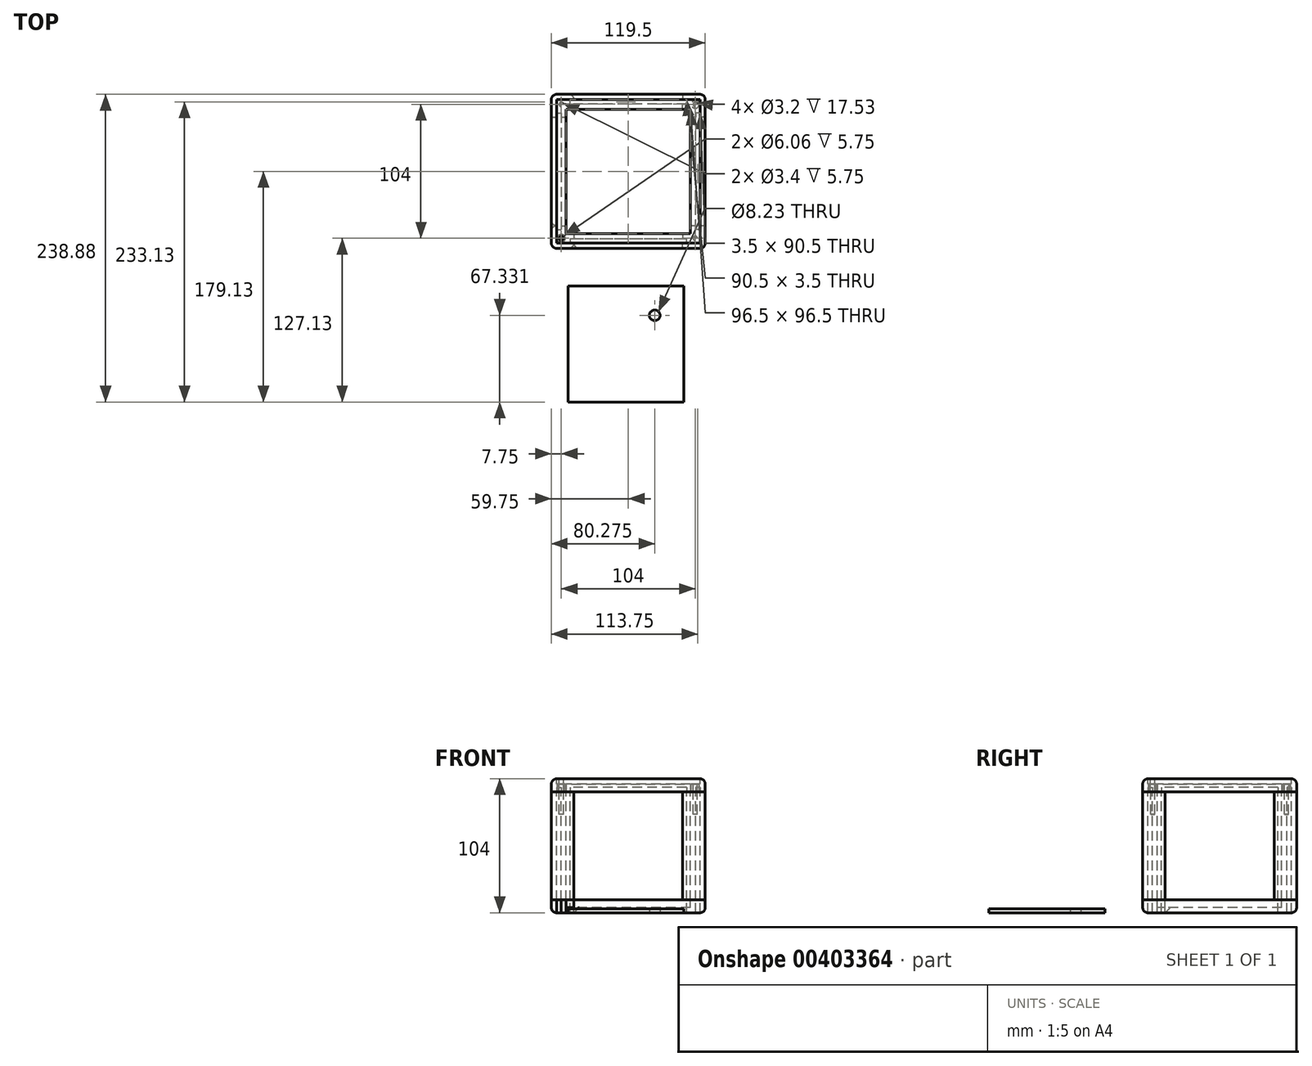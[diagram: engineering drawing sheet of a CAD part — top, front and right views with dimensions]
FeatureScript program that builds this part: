
annotation { "Feature Type Name" : "Feature", "Feature Type Description" : "" }
export const myFeature = defineFeature(function(context is Context, id is Id, definition is map)
    precondition{}
    {
        {
            assignVariable(context, id + "F0", {"name" : "lithophaneHeight", "anyValue" : 90});
        }
        {
            assignVariable(context, id + "F1", {"name" : "lithophaneThickness", "anyValue" : 3});
        }
        {
            assignVariable(context, id + "F2", {"name" : "lithophaneBorderWidth", "anyValue" : 3});
        }
        {
            assignVariable(context, id + "F3", {"name" : "slotToleranceWidth", "anyValue" : .5});
        }
        {
            assignVariable(context, id + "F4", {"name" : "shellThickness", "anyValue" : 4});
        }
        {
            assignVariable(context, id + "F5", {"name" : "baseThickness", "anyValue" : 10});
        }
        {
            assignVariable(context, id + "F6", {"name" : "topThickness", "anyValue" : getVariable(context, 'baseThickness')});
        }
        {
            assignVariable(context, id + "F7", {"name" : "MainEdgeFilletRadius", "anyValue" : 4});
        }
        {
            assignVariable(context, id + "F8", {"name" : "screwThreadDepth", "anyValue" : 19.53});
        }
        {
            assignVariable(context, id + "F9", {"name" : "screwHeadDepth", "anyValue" : 3});
        }
        {
            assignVariable(context, id + "F10", {"name" : "screwHeadRecessTolerance", "anyValue" : 1});
        }
        {
            assignVariable(context, id + "F11", {"name" : "screwHeadSupportThickness", "anyValue" : .25});
        }
        {
            assignVariable(context, id + "F12", {"name" : "screwThreadExtraDepth", "anyValue" : 5});
        }
        {
            var Q0;
            Q0=qCreatedBy(makeId("Top.planeOp"),FACE);
            var sketch = newSketch(context, id + "F13", { "sketchPlane" : qUnion([Q0])});
            skLineSegment(sketch, "E0.bottom", {"start": v(59.75, 59.75) * mm, "end": v(-59.75, 59.75) * mm});
            skLineSegment(sketch, "E0.top", {"start": v(59.75, -59.75) * mm, "end": v(-59.75, -59.75) * mm});
            skLineSegment(sketch, "E0.left", {"start": v(59.75, 59.75) * mm, "end": v(59.75, -59.75) * mm});
            skLineSegment(sketch, "E0.right", {"start": v(-59.75, 59.75) * mm, "end": v(-59.75, -59.75) * mm});
            skPoint(sketch, "E0.middle", {"position": v(0, 0) * mm});
            skSolve(sketch);
        }
        {
            var Q0;
            Q0=makeQuery(id+"F13.imprint","IMPRINT",FACE,{"disambiguationData":[TD([[makeQuery(id+"F13.imprint","IMPRINT",EDGE,{"derivedFrom":sQuery(id+"F13.wireOp",EDGE,"E0.bottom")}),1.0]])]});
            extrude(context, id + "F14", {"entities" : qUnion([Q0]), "depth" : (getVariable(context, 'lithophaneHeight') - (getVariable(context, 'lithophaneBorderWidth') * 2)) * mm});
        }
        {
            var Q0;
            Q0=makeQuery(id+"F14.opExtrude","CAP_FACE",FACE,{"disambiguationData":[OSD([sQuery(id+"F13.wireOp",EDGE,"E0.bottom"),sQuery(id+"F13.wireOp",EDGE,"E0.top"),sQuery(id+"F13.wireOp",EDGE,"E0.left"),sQuery(id+"F13.wireOp",EDGE,"E0.right")])],"isStart":false});
            var sketch = newSketch(context, id + "F15", { "sketchPlane" : qUnion([Q0])});
            skLineSegment(sketch, "E1", {"start": v(-55.75, -59.75) * mm, "end": v(-55.75, 59.75) * mm, "construction": true});
            skLineSegment(sketch, "E2", {"start": v(55.75, -59.75) * mm, "end": v(55.75, 59.75) * mm, "construction": true});
            skLineSegment(sketch, "E3", {"start": v(-59.75, 55.75) * mm, "end": v(59.75, 55.75) * mm, "construction": true});
            skLineSegment(sketch, "E4", {"start": v(-59.75, -55.75) * mm, "end": v(59.75, -55.75) * mm, "construction": true});
            skLineSegment(sketch, "E5", {"start": v(-59.75, 52.25) * mm, "end": v(59.75, 52.25) * mm, "construction": true});
            skLineSegment(sketch, "E6", {"start": v(-59.75, -52.25) * mm, "end": v(59.75, -52.25) * mm, "construction": true});
            skLineSegment(sketch, "E7", {"start": v(52.25, 59.75) * mm, "end": v(52.25, -59.75) * mm, "construction": true});
            skLineSegment(sketch, "E8", {"start": v(-52.25, 59.75) * mm, "end": v(-52.25, -59.75) * mm, "construction": true});
            skLineSegment(sketch, "E9", {"start": v(0, 59.75) * mm, "end": v(0, -59.75) * mm, "construction": true});
            skLineSegment(sketch, "E10", {"start": v(-59.75, 0) * mm, "end": v(59.75, 0) * mm, "construction": true});
            skLineSegment(sketch, "E11", {"start": v(-55.75, 45.25) * mm, "end": v(-52.25, 45.25) * mm});
            skLineSegment(sketch, "E12", {"start": v(-55.75, -45.25) * mm, "end": v(-52.25, -45.25) * mm});
            skPoint(sketch, "E13", {"position": v(-52.25, 0) * mm});
            skPoint(sketch, "E14", {"position": v(-55.75, 0) * mm});
            skLineSegment(sketch, "E15", {"start": v(-55.75, 45.25) * mm, "end": v(-55.75, -45.25) * mm});
            skLineSegment(sketch, "E16", {"start": v(-52.25, 45.25) * mm, "end": v(-52.25, -45.25) * mm});
            skLineSegment(sketch, "E17.MirrorCS", {"start": v(55.75, 45.25) * mm, "end": v(52.25, 45.25) * mm});
            skLineSegment(sketch, "E18.MirrorCS", {"start": v(55.75, -45.25) * mm, "end": v(52.25, -45.25) * mm});
            skLineSegment(sketch, "E19", {"start": v(-45.25, -52.25) * mm, "end": v(-45.25, -55.75) * mm});
            skLineSegment(sketch, "E20", {"start": v(45.25, -55.75) * mm, "end": v(45.25, -52.25) * mm});
            skLineSegment(sketch, "E21.MirrorCS", {"start": v(-45.25, 52.25) * mm, "end": v(-45.25, 55.75) * mm});
            skLineSegment(sketch, "E22.MirrorCS", {"start": v(45.25, 55.75) * mm, "end": v(45.25, 52.25) * mm});
            skLineSegment(sketch, "E23", {"start": v(-45.25, 52.25) * mm, "end": v(45.25, 52.25) * mm});
            skLineSegment(sketch, "E24", {"start": v(-45.25, 55.75) * mm, "end": v(45.25, 55.75) * mm});
            skLineSegment(sketch, "E25", {"start": v(52.25, 45.25) * mm, "end": v(52.25, -45.25) * mm});
            skLineSegment(sketch, "E26", {"start": v(55.75, 45.25) * mm, "end": v(55.75, -45.25) * mm});
            skLineSegment(sketch, "E27", {"start": v(-45.25, -52.25) * mm, "end": v(45.25, -52.25) * mm});
            skLineSegment(sketch, "E28", {"start": v(45.25, -55.75) * mm, "end": v(-45.25, -55.75) * mm});
            skLineSegment(sketch, "E29", {"start": v(-59.75, -42.25) * mm, "end": v(-55.75, -42.25) * mm});
            skLineSegment(sketch, "E30", {"start": v(-59.75, 42.25) * mm, "end": v(-55.75, 42.25) * mm});
            skLineSegment(sketch, "E31", {"start": v(-42.25, -59.75) * mm, "end": v(-42.25, -55.75) * mm});
            skLineSegment(sketch, "E32", {"start": v(42.25, -59.75) * mm, "end": v(42.25, -55.75) * mm});
            skLineSegment(sketch, "E33.MirrorCS", {"start": v(-42.25, 59.75) * mm, "end": v(-42.25, 55.75) * mm});
            skLineSegment(sketch, "E34.MirrorCS", {"start": v(42.25, 59.75) * mm, "end": v(42.25, 55.75) * mm});
            skLineSegment(sketch, "E35.MirrorCS", {"start": v(59.75, 42.25) * mm, "end": v(55.75, 42.25) * mm});
            skLineSegment(sketch, "E36.MirrorCS", {"start": v(59.75, -42.25) * mm, "end": v(55.75, -42.25) * mm});
            skLineSegment(sketch, "E37", {"start": v(-52.25, 42.25) * mm, "end": v(-48.25, 42.25) * mm});
            skLineSegment(sketch, "E38", {"start": v(-48.25, 42.25) * mm, "end": v(-48.25, 48.25) * mm});
            skLineSegment(sketch, "E39", {"start": v(-48.25, 48.25) * mm, "end": v(-42.25, 48.25) * mm});
            skLineSegment(sketch, "E40", {"start": v(-42.25, 48.25) * mm, "end": v(-42.25, 52.25) * mm});
            skLineSegment(sketch, "E41.MirrorCS", {"start": v(42.25, 48.25) * mm, "end": v(42.25, 52.25) * mm});
            skLineSegment(sketch, "E42.MirrorCS", {"start": v(48.25, 48.25) * mm, "end": v(42.25, 48.25) * mm});
            skLineSegment(sketch, "E43.MirrorCS", {"start": v(52.25, 42.25) * mm, "end": v(48.25, 42.25) * mm});
            skLineSegment(sketch, "E44.MirrorCS", {"start": v(48.25, 42.25) * mm, "end": v(48.25, 48.25) * mm});
            skLineSegment(sketch, "E45.MirrorCS", {"start": v(52.25, -42.25) * mm, "end": v(48.25, -42.25) * mm});
            skLineSegment(sketch, "E46.MirrorCS", {"start": v(48.25, -42.25) * mm, "end": v(48.25, -48.25) * mm});
            skLineSegment(sketch, "E47.MirrorCS", {"start": v(48.25, -48.25) * mm, "end": v(42.25, -48.25) * mm});
            skLineSegment(sketch, "E48.MirrorCS", {"start": v(42.25, -48.25) * mm, "end": v(42.25, -52.25) * mm});
            skLineSegment(sketch, "E49.MirrorCS", {"start": v(-42.25, -48.25) * mm, "end": v(-42.25, -52.25) * mm});
            skLineSegment(sketch, "E50.MirrorCS", {"start": v(-48.25, -42.25) * mm, "end": v(-48.25, -48.25) * mm});
            skLineSegment(sketch, "E51.MirrorCS", {"start": v(-52.25, -42.25) * mm, "end": v(-48.25, -42.25) * mm});
            skLineSegment(sketch, "E52.MirrorCS", {"start": v(-48.25, -48.25) * mm, "end": v(-42.25, -48.25) * mm});
            skSolve(sketch);
        }
        {
            var Q0;
            {var subQ4=sQuery(id+"F15.wireOp",EDGE,"E37");Q0=makeQuery(id+"F15.imprint","IMPRINT",FACE,{"disambiguationData":[TD([[makeQuery(id+"F15.imprint","IMPRINT",EDGE,{"derivedFrom":subQ4}),-1.0]])]});}
            var Q1;
            {var subQ3=sQuery(id+"F15.wireOp",EDGE,"E21.MirrorCS");Q1=makeQuery(id+"F15.imprint","IMPRINT",FACE,{"disambiguationData":[TD([[makeQuery(id+"F15.imprint","IMPRINT",EDGE,{"derivedFrom":subQ3}),-1.0]])]});}
            var Q2;
            {var subQ0=sQuery(id+"F15.wireOp",EDGE,"E33.MirrorCS");Q2=makeQuery(id+"F15.imprint","IMPRINT",FACE,{"disambiguationData":[TD([[makeQuery(id+"F15.imprint","IMPRINT",EDGE,{"derivedFrom":subQ0}),1.0]])]});}
            var Q3;
            {var subQ3=sQuery(id+"F15.wireOp",EDGE,"E17.MirrorCS");Q3=makeQuery(id+"F15.imprint","IMPRINT",FACE,{"disambiguationData":[TD([[makeQuery(id+"F15.imprint","IMPRINT",EDGE,{"derivedFrom":subQ3}),1.0]])]});}
            var Q4;
            {var subQ0=sQuery(id+"F15.wireOp",EDGE,"E35.MirrorCS");Q4=makeQuery(id+"F15.imprint","IMPRINT",FACE,{"disambiguationData":[TD([[makeQuery(id+"F15.imprint","IMPRINT",EDGE,{"derivedFrom":subQ0}),1.0]])]});}
            var Q5;
            {var subQ3=sQuery(id+"F15.wireOp",EDGE,"E19");Q5=makeQuery(id+"F15.imprint","IMPRINT",FACE,{"disambiguationData":[TD([[makeQuery(id+"F15.imprint","IMPRINT",EDGE,{"derivedFrom":subQ3}),1.0]])]});}
            var Q6;
            {var subQ0=sQuery(id+"F15.wireOp",EDGE,"E31");Q6=makeQuery(id+"F15.imprint","IMPRINT",FACE,{"disambiguationData":[TD([[makeQuery(id+"F15.imprint","IMPRINT",EDGE,{"derivedFrom":subQ0}),-1.0]])]});}
            var Q7;
            {var subQ0=sQuery(id+"F15.wireOp",EDGE,"E29");Q7=makeQuery(id+"F15.imprint","IMPRINT",FACE,{"disambiguationData":[TD([[makeQuery(id+"F15.imprint","IMPRINT",EDGE,{"derivedFrom":subQ0}),1.0]])]});}
            var Q8;
            {var subQ3=sQuery(id+"F15.wireOp",EDGE,"E11");Q8=makeQuery(id+"F15.imprint","IMPRINT",FACE,{"disambiguationData":[TD([[makeQuery(id+"F15.imprint","IMPRINT",EDGE,{"derivedFrom":subQ3}),-1.0]])]});}
            extrude(context, id + "F16", {"entities" : qUnion([Q0, Q1, Q2, Q3, Q4, Q5, Q6, Q7, Q8]), "operationType" : NewBodyOperationType.REMOVE, "oppositeDirection" : true, "depth" : (getVariable(context, 'lithophaneHeight') + getVariable(context, 'slotToleranceWidth')) * mm});
        }
        {
            var Q0;
            {var subQ2=sQuery(id+"F15.wireOp",EDGE,"E12");var subQ7=sQuery(id+"F13.wireOp",EDGE,"E0.top");var subQ10=sQuery(id+"F13.wireOp",EDGE,"E0.right");Q0=makeQuery(id+"F16.boolean.opBoolean","SPLIT",FACE,{"disambiguationData":[TD([makeQuery(id+"F16.opExtrude","SWEPT_FACE",FACE,{"disambiguationData":[OSD([subQ2])]})])],"derivedFrom":makeQuery(id+"F14.opExtrude","CAP_FACE",FACE,{"disambiguationData":[OSD([sQuery(id+"F13.wireOp",EDGE,"E0.bottom"),subQ7,sQuery(id+"F13.wireOp",EDGE,"E0.left"),subQ10])],"isStart":true})});}
            var sketch = newSketch(context, id + "F17", { "sketchPlane" : qUnion([Q0])});
            skLineSegment(sketch, "E53.0", {"start": v(59.75, -59.75) * mm, "end": v(59.75, -42.25) * mm});
            skLineSegment(sketch, "E53.1", {"start": v(59.75, -59.75) * mm, "end": v(42.25, -59.75) * mm});
            skLineSegment(sketch, "E54.0", {"start": v(59.75, 42.25) * mm, "end": v(59.75, 59.75) * mm});
            skLineSegment(sketch, "E54.1", {"start": v(59.75, 59.75) * mm, "end": v(42.25, 59.75) * mm});
            skLineSegment(sketch, "E54.2", {"start": v(-42.25, 59.75) * mm, "end": v(-59.75, 59.75) * mm});
            skLineSegment(sketch, "E54.3", {"start": v(-59.75, 42.25) * mm, "end": v(-59.75, 59.75) * mm});
            skLineSegment(sketch, "E54.4", {"start": v(-59.75, -59.75) * mm, "end": v(-59.75, -42.25) * mm});
            skLineSegment(sketch, "E54.5", {"start": v(-42.25, -59.75) * mm, "end": v(-59.75, -59.75) * mm});
            skLineSegment(sketch, "E55.bottom", {"start": v(-59.75, 59.75) * mm, "end": v(59.75, 59.75) * mm});
            skLineSegment(sketch, "E55.top", {"start": v(-59.75, -59.75) * mm, "end": v(59.75, -59.75) * mm});
            skLineSegment(sketch, "E55.left", {"start": v(-59.75, 59.75) * mm, "end": v(-59.75, -59.75) * mm});
            skLineSegment(sketch, "E55.right", {"start": v(59.75, 59.75) * mm, "end": v(59.75, -59.75) * mm});
            skLineSegment(sketch, "E56.0", {"start": v(-55.75, 42.25) * mm, "end": v(-55.75, 45.25) * mm});
            skLineSegment(sketch, "E56.1", {"start": v(-55.75, 45.25) * mm, "end": v(-52.25, 45.25) * mm});
            skLineSegment(sketch, "E56.2", {"start": v(-52.25, 42.25) * mm, "end": v(-52.25, 45.25) * mm});
            skLineSegment(sketch, "E57.0", {"start": v(-45.25, 52.25) * mm, "end": v(-42.25, 52.25) * mm});
            skLineSegment(sketch, "E57.1", {"start": v(-45.25, 52.25) * mm, "end": v(-45.25, 55.75) * mm});
            skLineSegment(sketch, "E57.2", {"start": v(-42.25, 55.75) * mm, "end": v(-45.25, 55.75) * mm});
            skLineSegment(sketch, "E58.0", {"start": v(45.25, 55.75) * mm, "end": v(42.25, 55.75) * mm});
            skLineSegment(sketch, "E59.0", {"start": v(45.25, 55.75) * mm, "end": v(45.25, 52.25) * mm});
            skLineSegment(sketch, "E60.0", {"start": v(42.25, 52.25) * mm, "end": v(45.25, 52.25) * mm});
            skLineSegment(sketch, "E61.0", {"start": v(55.75, 45.25) * mm, "end": v(52.25, 45.25) * mm});
            skLineSegment(sketch, "E62.0", {"start": v(52.25, 42.25) * mm, "end": v(52.25, 45.25) * mm});
            skLineSegment(sketch, "E62.1", {"start": v(55.75, 42.25) * mm, "end": v(55.75, 45.25) * mm});
            skLineSegment(sketch, "E63.0", {"start": v(55.75, -45.25) * mm, "end": v(55.75, -42.25) * mm});
            skLineSegment(sketch, "E63.1", {"start": v(55.75, -45.25) * mm, "end": v(52.25, -45.25) * mm});
            skLineSegment(sketch, "E63.2", {"start": v(52.25, -45.25) * mm, "end": v(52.25, -42.25) * mm});
            skLineSegment(sketch, "E63.3", {"start": v(42.25, -52.25) * mm, "end": v(45.25, -52.25) * mm});
            skLineSegment(sketch, "E63.4", {"start": v(45.25, -55.75) * mm, "end": v(45.25, -52.25) * mm});
            skLineSegment(sketch, "E63.5", {"start": v(42.25, -55.75) * mm, "end": v(45.25, -55.75) * mm});
            skLineSegment(sketch, "E63.6", {"start": v(-45.25, -55.75) * mm, "end": v(-42.25, -55.75) * mm});
            skLineSegment(sketch, "E63.7", {"start": v(-45.25, -52.25) * mm, "end": v(-42.25, -52.25) * mm});
            skLineSegment(sketch, "E63.8", {"start": v(-52.25, -45.25) * mm, "end": v(-52.25, -42.25) * mm});
            skLineSegment(sketch, "E63.9", {"start": v(-55.75, -45.25) * mm, "end": v(-52.25, -45.25) * mm});
            skLineSegment(sketch, "E63.10", {"start": v(-55.75, -45.25) * mm, "end": v(-55.75, -42.25) * mm});
            skLineSegment(sketch, "E63.11", {"start": v(-45.25, -52.25) * mm, "end": v(-45.25, -55.75) * mm});
            skLineSegment(sketch, "E64.bottom", {"start": v(-45.25, 55.75) * mm, "end": v(45.25, 55.75) * mm});
            skLineSegment(sketch, "E64.top", {"start": v(-45.25, 52.25) * mm, "end": v(45.25, 52.25) * mm});
            skLineSegment(sketch, "E64.left", {"start": v(-45.25, 55.75) * mm, "end": v(-45.25, 52.25) * mm});
            skLineSegment(sketch, "E65.bottom", {"start": v(52.25, 45.25) * mm, "end": v(55.75, 45.25) * mm});
            skLineSegment(sketch, "E65.top", {"start": v(52.25, -45.25) * mm, "end": v(55.75, -45.25) * mm});
            skLineSegment(sketch, "E65.left", {"start": v(52.25, 45.25) * mm, "end": v(52.25, -45.25) * mm});
            skLineSegment(sketch, "E65.right", {"start": v(55.75, 45.25) * mm, "end": v(55.75, -45.25) * mm});
            skLineSegment(sketch, "E66.bottom", {"start": v(45.25, -52.25) * mm, "end": v(-45.25, -52.25) * mm});
            skLineSegment(sketch, "E66.top", {"start": v(45.25, -55.75) * mm, "end": v(-45.25, -55.75) * mm});
            skLineSegment(sketch, "E66.left", {"start": v(45.25, -52.25) * mm, "end": v(45.25, -55.75) * mm});
            skLineSegment(sketch, "E67.bottom", {"start": v(-52.25, -45.25) * mm, "end": v(-55.75, -45.25) * mm});
            skLineSegment(sketch, "E67.top", {"start": v(-52.25, 45.25) * mm, "end": v(-55.75, 45.25) * mm});
            skLineSegment(sketch, "E67.left", {"start": v(-52.25, -45.25) * mm, "end": v(-52.25, 45.25) * mm});
            skLineSegment(sketch, "E67.right", {"start": v(-55.75, -45.25) * mm, "end": v(-55.75, 45.25) * mm});
            skLineSegment(sketch, "E68.bottom", {"start": v(48.25, -48.25) * mm, "end": v(-48.25, -48.25) * mm});
            skLineSegment(sketch, "E68.top", {"start": v(48.25, 48.25) * mm, "end": v(-48.25, 48.25) * mm});
            skLineSegment(sketch, "E68.left", {"start": v(48.25, -48.25) * mm, "end": v(48.25, 48.25) * mm});
            skLineSegment(sketch, "E68.right", {"start": v(-48.25, -48.25) * mm, "end": v(-48.25, 48.25) * mm});
            skPoint(sketch, "E68.middle", {"position": v(0, 0) * mm});
            skSolve(sketch);
        }
        {
            var Q0;
            {var subQ6=sQuery(id+"F17.wireOp",EDGE,"E64.left");Q0=makeQuery(id+"F17.imprint","IMPRINT",FACE,{"disambiguationData":[TD([[makeQuery(id+"F17.imprint","IMPRINT",EDGE,{"derivedFrom":subQ6}),1.0]])]});}
            var Q1;
            {var subQ24=sQuery(id+"F17.wireOp",EDGE,"E59.0");Q1=makeQuery(id+"F17.imprint","IMPRINT",FACE,{"disambiguationData":[TD([[makeQuery(id+"F17.imprint","IMPRINT",EDGE,{"derivedFrom":subQ24}),1.0]])]});}
            var Q2;
            Q2=makeQuery(id+"F17.imprint","IMPRINT",FACE,{"disambiguationData":[TD([[makeQuery(id+"F17.imprint","IMPRINT",EDGE,{"derivedFrom":sQuery(id+"F17.wireOp",EDGE,"E68.bottom")}),-1.0]])]});
            extrude(context, id + "F18", {"entities" : qUnion([Q0, Q1, Q2]), "depth" : (getVariable(context, 'lithophaneBorderWidth') + getVariable(context, 'slotToleranceWidth')) * mm});
        }
        {
            var Q0;
            Q0=makeQuery(id+"F18.opExtrude","CAP_FACE",FACE,{"disambiguationData":[OSD([sQuery(id+"F17.wireOp",EDGE,"E55.bottom"),sQuery(id+"F17.wireOp",EDGE,"E55.top"),sQuery(id+"F17.wireOp",EDGE,"E55.left"),sQuery(id+"F17.wireOp",EDGE,"E55.right"),sQuery(id+"F17.wireOp",EDGE,"E64.bottom"),sQuery(id+"F17.wireOp",EDGE,"E64.top"),sQuery(id+"F17.wireOp",EDGE,"E64.left"),sQuery(id+"F17.wireOp",EDGE,"E59.0"),sQuery(id+"F17.wireOp",EDGE,"E65.bottom"),sQuery(id+"F17.wireOp",EDGE,"E65.top"),sQuery(id+"F17.wireOp",EDGE,"E65.left"),sQuery(id+"F17.wireOp",EDGE,"E65.right"),sQuery(id+"F17.wireOp",EDGE,"E66.bottom"),sQuery(id+"F17.wireOp",EDGE,"E66.top"),sQuery(id+"F17.wireOp",EDGE,"E66.left"),sQuery(id+"F17.wireOp",EDGE,"E63.11"),sQuery(id+"F17.wireOp",EDGE,"E67.bottom"),sQuery(id+"F17.wireOp",EDGE,"E67.top"),sQuery(id+"F17.wireOp",EDGE,"E67.left"),sQuery(id+"F17.wireOp",EDGE,"E67.right")])],"isStart":false});
            var sketch = newSketch(context, id + "F19", { "sketchPlane" : qUnion([Q0])});
            skLineSegment(sketch, "E69.bottom", {"start": v(-59.75, 59.75) * mm, "end": v(59.75, 59.75) * mm});
            skLineSegment(sketch, "E69.top", {"start": v(-59.75, -59.75) * mm, "end": v(59.75, -59.75) * mm});
            skLineSegment(sketch, "E69.left", {"start": v(-59.75, 59.75) * mm, "end": v(-59.75, -59.75) * mm});
            skLineSegment(sketch, "E69.right", {"start": v(59.75, 59.75) * mm, "end": v(59.75, -59.75) * mm});
            skSolve(sketch);
        }
        {
            var Q0;
            Q0=makeQuery(id+"F19.imprint","IMPRINT",FACE,{"disambiguationData":[TD([[makeQuery(id+"F19.imprint","IMPRINT",EDGE,{"derivedFrom":sQuery(id+"F19.wireOp",EDGE,"E69.bottom")}),1.0]])]});
            var Q1;
            Q1=makeQuery(id+"F19.imprint","IMPRINT",FACE,{"disambiguationData":[TD([[makeQuery(id+"F19.imprint","IMPRINT",EDGE,{"derivedFrom":makeQuery(id+"F18.opExtrude","CAP_EDGE",EDGE,{"disambiguationData":[OSD([sQuery(id+"F17.wireOp",EDGE,"E67.bottom")])],"isStart":false})}),-1.0]])]});
            var Q2;
            Q2=makeQuery(id+"F19.imprint","IMPRINT",FACE,{"disambiguationData":[TD([[makeQuery(id+"F19.imprint","IMPRINT",EDGE,{"derivedFrom":makeQuery(id+"F18.opExtrude","CAP_EDGE",EDGE,{"disambiguationData":[OSD([sQuery(id+"F17.wireOp",EDGE,"E66.bottom")])],"isStart":false})}),1.0]])]});
            var Q3;
            Q3=makeQuery(id+"F19.imprint","IMPRINT",FACE,{"disambiguationData":[TD([[makeQuery(id+"F19.imprint","IMPRINT",EDGE,{"derivedFrom":makeQuery(id+"F18.opExtrude","CAP_EDGE",EDGE,{"disambiguationData":[OSD([sQuery(id+"F17.wireOp",EDGE,"E65.bottom")])],"isStart":false})}),-1.0]])]});
            var Q4;
            Q4=makeQuery(id+"F19.imprint","IMPRINT",FACE,{"disambiguationData":[TD([[makeQuery(id+"F19.imprint","IMPRINT",EDGE,{"derivedFrom":makeQuery(id+"F18.opExtrude","CAP_EDGE",EDGE,{"disambiguationData":[OSD([sQuery(id+"F17.wireOp",EDGE,"E64.bottom")])],"isStart":false})}),1.0]])]});
            extrude(context, id + "F20", {"entities" : qUnion([Q0, Q1, Q2, Q3, Q4]), "operationType" : NewBodyOperationType.ADD, "depth" : (10 - getVariable(context, 'lithophaneBorderWidth') - getVariable(context, 'slotToleranceWidth')) * mm});
        }
        {
            var Q0;
            {var subQ1=sQuery(id+"F15.wireOp",EDGE,"E17.MirrorCS");var subQ10=sQuery(id+"F13.wireOp",EDGE,"E0.bottom");var subQ11=sQuery(id+"F13.wireOp",EDGE,"E0.left");Q0=makeQuery(id+"F16.boolean.opBoolean","SPLIT",FACE,{"disambiguationData":[TD([makeQuery(id+"F16.opExtrude","SWEPT_FACE",FACE,{"disambiguationData":[OSD([subQ1])]})])],"derivedFrom":makeQuery(id+"F14.opExtrude","CAP_FACE",FACE,{"disambiguationData":[OSD([subQ10,sQuery(id+"F13.wireOp",EDGE,"E0.top"),subQ11,sQuery(id+"F13.wireOp",EDGE,"E0.right")])],"isStart":false})});}
            var sketch = newSketch(context, id + "F21", { "sketchPlane" : qUnion([Q0])});
            skLineSegment(sketch, "E70.0", {"start": v(45.25, 52.25) * mm, "end": v(-45.25, 52.25) * mm});
            skLineSegment(sketch, "E70.1", {"start": v(45.25, 55.75) * mm, "end": v(-45.25, 55.75) * mm});
            skLineSegment(sketch, "E70.2", {"start": v(45.25, 55.75) * mm, "end": v(45.25, 52.25) * mm});
            skLineSegment(sketch, "E70.3", {"start": v(-45.25, 52.25) * mm, "end": v(-45.25, 55.75) * mm});
            skLineSegment(sketch, "E71.0", {"start": v(-52.25, 45.25) * mm, "end": v(-52.25, -45.25) * mm});
            skLineSegment(sketch, "E71.1", {"start": v(-55.75, 45.25) * mm, "end": v(-55.75, -45.25) * mm});
            skLineSegment(sketch, "E71.2", {"start": v(-55.75, 45.25) * mm, "end": v(-52.25, 45.25) * mm});
            skLineSegment(sketch, "E71.3", {"start": v(-55.75, -45.25) * mm, "end": v(-52.25, -45.25) * mm});
            skLineSegment(sketch, "E72.0", {"start": v(45.25, -55.75) * mm, "end": v(-45.25, -55.75) * mm});
            skLineSegment(sketch, "E72.1", {"start": v(-45.25, -52.25) * mm, "end": v(45.25, -52.25) * mm});
            skLineSegment(sketch, "E73.0", {"start": v(45.25, -55.75) * mm, "end": v(45.25, -52.25) * mm});
            skLineSegment(sketch, "E74.0", {"start": v(-45.25, -52.25) * mm, "end": v(-45.25, -55.75) * mm});
            skLineSegment(sketch, "E75.0", {"start": v(52.25, -45.25) * mm, "end": v(52.25, 45.25) * mm});
            skLineSegment(sketch, "E75.1", {"start": v(55.75, -45.25) * mm, "end": v(55.75, 45.25) * mm});
            skLineSegment(sketch, "E75.2", {"start": v(55.75, 45.25) * mm, "end": v(52.25, 45.25) * mm});
            skLineSegment(sketch, "E75.3", {"start": v(55.75, -45.25) * mm, "end": v(52.25, -45.25) * mm});
            skLineSegment(sketch, "E76.0", {"start": v(-59.75, 59.75) * mm, "end": v(59.75, 59.75) * mm});
            skLineSegment(sketch, "E77.0", {"start": v(59.75, -59.75) * mm, "end": v(59.75, 59.75) * mm});
            skLineSegment(sketch, "E78.0", {"start": v(59.75, -59.75) * mm, "end": v(-59.75, -59.75) * mm});
            skLineSegment(sketch, "E79.0", {"start": v(-59.75, 59.75) * mm, "end": v(-59.75, -59.75) * mm});
            skSolve(sketch);
        }
        {
            var Q0;
            {var subQ10=sQuery(id+"F21.wireOp",EDGE,"E70.3");Q0=makeQuery(id+"F21.imprint","IMPRINT",FACE,{"disambiguationData":[TD([[makeQuery(id+"F21.imprint","IMPRINT",EDGE,{"derivedFrom":subQ10}),1.0]])]});}
            var Q1;
            {var subQ6=sQuery(id+"F21.wireOp",EDGE,"E70.2");Q1=makeQuery(id+"F21.imprint","IMPRINT",FACE,{"disambiguationData":[TD([[makeQuery(id+"F21.imprint","IMPRINT",EDGE,{"derivedFrom":subQ6}),1.0]])]});}
            extrude(context, id + "F22", {"entities" : qUnion([Q0, Q1]), "depth" : (getVariable(context, 'lithophaneBorderWidth') + getVariable(context, 'slotToleranceWidth')) * mm});
        }
        {
            var Q0;
            Q0=makeQuery(id+"F22.opExtrude","CAP_FACE",FACE,{"disambiguationData":[OSD([sQuery(id+"F21.wireOp",EDGE,"E70.0"),sQuery(id+"F21.wireOp",EDGE,"E70.1"),sQuery(id+"F21.wireOp",EDGE,"E70.2"),sQuery(id+"F21.wireOp",EDGE,"E70.3"),sQuery(id+"F21.wireOp",EDGE,"E71.0"),sQuery(id+"F21.wireOp",EDGE,"E71.1"),sQuery(id+"F21.wireOp",EDGE,"E71.2"),sQuery(id+"F21.wireOp",EDGE,"E71.3"),sQuery(id+"F21.wireOp",EDGE,"E72.0"),sQuery(id+"F21.wireOp",EDGE,"E72.1"),sQuery(id+"F21.wireOp",EDGE,"E73.0"),sQuery(id+"F21.wireOp",EDGE,"E74.0"),sQuery(id+"F21.wireOp",EDGE,"E75.0"),sQuery(id+"F21.wireOp",EDGE,"E75.1"),sQuery(id+"F21.wireOp",EDGE,"E75.2"),sQuery(id+"F21.wireOp",EDGE,"E75.3"),sQuery(id+"F21.wireOp",EDGE,"E76.0"),sQuery(id+"F21.wireOp",EDGE,"E77.0"),sQuery(id+"F21.wireOp",EDGE,"E78.0"),sQuery(id+"F21.wireOp",EDGE,"E79.0")])],"isStart":false});
            var sketch = newSketch(context, id + "F23", { "sketchPlane" : qUnion([Q0])});
            skLineSegment(sketch, "E80.bottom", {"start": v(-59.75, 59.75) * mm, "end": v(59.75, 59.75) * mm});
            skLineSegment(sketch, "E80.top", {"start": v(-59.75, -59.75) * mm, "end": v(59.75, -59.75) * mm});
            skLineSegment(sketch, "E80.left", {"start": v(-59.75, 59.75) * mm, "end": v(-59.75, -59.75) * mm});
            skLineSegment(sketch, "E80.right", {"start": v(59.75, 59.75) * mm, "end": v(59.75, -59.75) * mm});
            skSolve(sketch);
        }
        {
            var Q0;
            Q0 = qSketchRegion(id + "F23", true);
            extrude(context, id + "F24", {"entities" : qUnion([Q0]), "operationType" : NewBodyOperationType.ADD, "depth" : (10 - getVariable(context, 'lithophaneBorderWidth') - getVariable(context, 'slotToleranceWidth')) * mm});
        }
        {
            var Q0;
            Q0=makeQuery(id+"F24.boolean.opBoolean","MERGE",EDGE,{"derivedFrom":[makeQuery(id+"F22.opExtrude","SWEPT_EDGE",EDGE,{"disambiguationData":[OSD([sQuery(id+"F21.wireOp",EDGE,"E78.0"),sQuery(id+"F21.wireOp",EDGE,"E79.0")])]}),makeQuery(id+"F24.opExtrude","SWEPT_EDGE",EDGE,{"disambiguationData":[OSD([sQuery(id+"F23.wireOp",EDGE,"E80.top"),sQuery(id+"F23.wireOp",EDGE,"E80.left")])]})]});
            var Q1;
            Q1=makeQuery(id+"F14.opExtrude","SWEPT_EDGE",EDGE,{"disambiguationData":[OSD([sQuery(id+"F13.wireOp",EDGE,"E0.top"),sQuery(id+"F13.wireOp",EDGE,"E0.right")])]});
            var Q2;
            Q2=makeQuery(id+"F20.boolean.opBoolean","MERGE",EDGE,{"derivedFrom":[makeQuery(id+"F18.opExtrude","SWEPT_EDGE",EDGE,{"disambiguationData":[OSD([sQuery(id+"F17.wireOp",EDGE,"E55.bottom"),sQuery(id+"F17.wireOp",EDGE,"E55.left")])]}),makeQuery(id+"F20.opExtrude","SWEPT_EDGE",EDGE,{"disambiguationData":[OSD([sQuery(id+"F19.wireOp",EDGE,"E69.bottom"),sQuery(id+"F19.wireOp",EDGE,"E69.left")])]})]});
            var Q3;
            Q3=makeQuery(id+"F20.opExtrude","CAP_EDGE",EDGE,{"disambiguationData":[OSD([sQuery(id+"F19.wireOp",EDGE,"E69.bottom")])],"isStart":false});
            var Q4;
            Q4=makeQuery(id+"F24.opExtrude","CAP_EDGE",EDGE,{"disambiguationData":[OSD([sQuery(id+"F23.wireOp",EDGE,"E80.top")])],"isStart":false});
            var Q5;
            Q5=makeQuery(id+"F14.opExtrude","SWEPT_EDGE",EDGE,{"disambiguationData":[OSD([sQuery(id+"F13.wireOp",EDGE,"E0.top"),sQuery(id+"F13.wireOp",EDGE,"E0.left")])]});
            var Q6;
            Q6=makeQuery(id+"F24.boolean.opBoolean","MERGE",EDGE,{"derivedFrom":[makeQuery(id+"F22.opExtrude","SWEPT_EDGE",EDGE,{"disambiguationData":[OSD([sQuery(id+"F21.wireOp",EDGE,"E77.0"),sQuery(id+"F21.wireOp",EDGE,"E78.0")])]}),makeQuery(id+"F24.opExtrude","SWEPT_EDGE",EDGE,{"disambiguationData":[OSD([sQuery(id+"F23.wireOp",EDGE,"E80.top"),sQuery(id+"F23.wireOp",EDGE,"E80.right")])]})]});
            var Q7;
            Q7=makeQuery(id+"F20.boolean.opBoolean","MERGE",EDGE,{"derivedFrom":[makeQuery(id+"F18.opExtrude","SWEPT_EDGE",EDGE,{"disambiguationData":[OSD([sQuery(id+"F17.wireOp",EDGE,"E55.bottom"),sQuery(id+"F17.wireOp",EDGE,"E55.right")])]}),makeQuery(id+"F20.opExtrude","SWEPT_EDGE",EDGE,{"disambiguationData":[OSD([sQuery(id+"F19.wireOp",EDGE,"E69.bottom"),sQuery(id+"F19.wireOp",EDGE,"E69.right")])]})]});
            var Q8;
            Q8=makeQuery(id+"F20.opExtrude","CAP_EDGE",EDGE,{"disambiguationData":[OSD([sQuery(id+"F19.wireOp",EDGE,"E69.right")])],"isStart":false});
            var Q9;
            Q9=makeQuery(id+"F24.opExtrude","CAP_EDGE",EDGE,{"disambiguationData":[OSD([sQuery(id+"F23.wireOp",EDGE,"E80.right")])],"isStart":false});
            var Q10;
            Q10=makeQuery(id+"F14.opExtrude","SWEPT_EDGE",EDGE,{"disambiguationData":[OSD([sQuery(id+"F13.wireOp",EDGE,"E0.bottom"),sQuery(id+"F13.wireOp",EDGE,"E0.left")])]});
            var Q11;
            Q11=makeQuery(id+"F24.boolean.opBoolean","MERGE",EDGE,{"derivedFrom":[makeQuery(id+"F22.opExtrude","SWEPT_EDGE",EDGE,{"disambiguationData":[OSD([sQuery(id+"F21.wireOp",EDGE,"E76.0"),sQuery(id+"F21.wireOp",EDGE,"E77.0")])]}),makeQuery(id+"F24.opExtrude","SWEPT_EDGE",EDGE,{"disambiguationData":[OSD([sQuery(id+"F23.wireOp",EDGE,"E80.bottom"),sQuery(id+"F23.wireOp",EDGE,"E80.right")])]})]});
            var Q12;
            Q12=makeQuery(id+"F20.boolean.opBoolean","MERGE",EDGE,{"derivedFrom":[makeQuery(id+"F18.opExtrude","SWEPT_EDGE",EDGE,{"disambiguationData":[OSD([sQuery(id+"F17.wireOp",EDGE,"E55.top"),sQuery(id+"F17.wireOp",EDGE,"E55.right")])]}),makeQuery(id+"F20.opExtrude","SWEPT_EDGE",EDGE,{"disambiguationData":[OSD([sQuery(id+"F19.wireOp",EDGE,"E69.top"),sQuery(id+"F19.wireOp",EDGE,"E69.right")])]})]});
            var Q13;
            Q13=makeQuery(id+"F24.opExtrude","CAP_EDGE",EDGE,{"disambiguationData":[OSD([sQuery(id+"F23.wireOp",EDGE,"E80.bottom")])],"isStart":false});
            var Q14;
            Q14=makeQuery(id+"F14.opExtrude","SWEPT_EDGE",EDGE,{"disambiguationData":[OSD([sQuery(id+"F13.wireOp",EDGE,"E0.bottom"),sQuery(id+"F13.wireOp",EDGE,"E0.right")])]});
            var Q15;
            Q15=makeQuery(id+"F24.boolean.opBoolean","MERGE",EDGE,{"derivedFrom":[makeQuery(id+"F22.opExtrude","SWEPT_EDGE",EDGE,{"disambiguationData":[OSD([sQuery(id+"F21.wireOp",EDGE,"E76.0"),sQuery(id+"F21.wireOp",EDGE,"E79.0")])]}),makeQuery(id+"F24.opExtrude","SWEPT_EDGE",EDGE,{"disambiguationData":[OSD([sQuery(id+"F23.wireOp",EDGE,"E80.bottom"),sQuery(id+"F23.wireOp",EDGE,"E80.left")])]})]});
            var Q16;
            Q16=makeQuery(id+"F20.boolean.opBoolean","MERGE",EDGE,{"derivedFrom":[makeQuery(id+"F18.opExtrude","SWEPT_EDGE",EDGE,{"disambiguationData":[OSD([sQuery(id+"F17.wireOp",EDGE,"E55.top"),sQuery(id+"F17.wireOp",EDGE,"E55.left")])]}),makeQuery(id+"F20.opExtrude","SWEPT_EDGE",EDGE,{"disambiguationData":[OSD([sQuery(id+"F19.wireOp",EDGE,"E69.top"),sQuery(id+"F19.wireOp",EDGE,"E69.left")])]})]});
            var Q17;
            Q17=makeQuery(id+"F24.opExtrude","CAP_EDGE",EDGE,{"disambiguationData":[OSD([sQuery(id+"F23.wireOp",EDGE,"E80.left")])],"isStart":false});
            var Q18;
            Q18=makeQuery(id+"F20.opExtrude","CAP_EDGE",EDGE,{"disambiguationData":[OSD([sQuery(id+"F19.wireOp",EDGE,"E69.left")])],"isStart":false});
            var Q19;
            Q19=makeQuery(id+"F20.opExtrude","CAP_EDGE",EDGE,{"disambiguationData":[OSD([sQuery(id+"F19.wireOp",EDGE,"E69.top")])],"isStart":false});
            var Q20;
            Q20=makeQuery(id+"F16.boolean.opBoolean","COPY",EDGE,{"derivedFrom":makeQuery(id+"F16.opExtrude","SWEPT_EDGE",EDGE,{"disambiguationData":[OSD([sQuery(id+"F13.wireOp",EDGE,"E0.top"),sQuery(id+"F15.wireOp",EDGE,"E31")])]})});
            var Q21;
            Q21=makeQuery(id+"F16.boolean.opBoolean","COPY",EDGE,{"derivedFrom":makeQuery(id+"F16.opExtrude","SWEPT_EDGE",EDGE,{"disambiguationData":[OSD([sQuery(id+"F13.wireOp",EDGE,"E0.top"),sQuery(id+"F15.wireOp",EDGE,"E32")])]})});
            var Q22;
            Q22=makeQuery(id+"F16.boolean.opBoolean","COPY",EDGE,{"derivedFrom":makeQuery(id+"F16.opExtrude","SWEPT_EDGE",EDGE,{"disambiguationData":[OSD([sQuery(id+"F13.wireOp",EDGE,"E0.right"),sQuery(id+"F15.wireOp",EDGE,"E29")])]})});
            var Q23;
            Q23=makeQuery(id+"F16.boolean.opBoolean","COPY",EDGE,{"derivedFrom":makeQuery(id+"F16.opExtrude","SWEPT_EDGE",EDGE,{"disambiguationData":[OSD([sQuery(id+"F13.wireOp",EDGE,"E0.right"),sQuery(id+"F15.wireOp",EDGE,"E30")])]})});
            var Q24;
            Q24=makeQuery(id+"F16.boolean.opBoolean","COPY",EDGE,{"derivedFrom":makeQuery(id+"F16.opExtrude","SWEPT_EDGE",EDGE,{"disambiguationData":[OSD([sQuery(id+"F13.wireOp",EDGE,"E0.bottom"),sQuery(id+"F15.wireOp",EDGE,"E33.MirrorCS")])]})});
            var Q25;
            Q25=makeQuery(id+"F16.boolean.opBoolean","COPY",EDGE,{"derivedFrom":makeQuery(id+"F16.opExtrude","SWEPT_EDGE",EDGE,{"disambiguationData":[OSD([sQuery(id+"F13.wireOp",EDGE,"E0.bottom"),sQuery(id+"F15.wireOp",EDGE,"E34.MirrorCS")])]})});
            fillet(context, id + "F25", {"entities" : qUnion([Q0, Q1, Q2, Q3, Q4, Q5, Q6, Q7, Q8, Q9, Q10, Q11, Q12, Q13, Q14, Q15, Q16, Q17, Q18, Q19, Q20, Q21, Q22, Q23, Q24, Q25]), "radius" : (getVariable(context, 'MainEdgeFilletRadius')) * mm, "tangentPropagation" : true, "allowEdgeOverflow" : false});
        }
        {
            var Q0;
            Q0=makeQuery(id+"F24.opExtrude","CAP_FACE",FACE,{"disambiguationData":[OSD([sQuery(id+"F23.wireOp",EDGE,"E80.bottom"),sQuery(id+"F23.wireOp",EDGE,"E80.top"),sQuery(id+"F23.wireOp",EDGE,"E80.left"),sQuery(id+"F23.wireOp",EDGE,"E80.right")])],"isStart":false});
            var sketch = newSketch(context, id + "F26", { "sketchPlane" : qUnion([Q0])});
            skLineSegment(sketch, "E81.0", {"start": v(55.75, 55.75) * mm, "end": v(-55.75, 55.75) * mm});
            skLineSegment(sketch, "E82.0", {"start": v(-55.75, 55.75) * mm, "end": v(-55.75, -55.75) * mm});
            skLineSegment(sketch, "E83.0", {"start": v(-48.25, 48.25) * mm, "end": v(-42.25, 48.25) * mm});
            skLineSegment(sketch, "E84.0", {"start": v(-48.25, 42.25) * mm, "end": v(-48.25, 48.25) * mm});
            skLineSegment(sketch, "E85.bottom", {"start": v(-48.25, 48.25) * mm, "end": v(-55.75, 48.25) * mm, "construction": true});
            skLineSegment(sketch, "E85.top", {"start": v(-48.25, 55.75) * mm, "end": v(-55.75, 55.75) * mm, "construction": true});
            skLineSegment(sketch, "E85.left", {"start": v(-48.25, 48.25) * mm, "end": v(-48.25, 55.75) * mm, "construction": true});
            skLineSegment(sketch, "E85.right", {"start": v(-55.75, 48.25) * mm, "end": v(-55.75, 55.75) * mm, "construction": true});
            skLineSegment(sketch, "E86.0", {"start": v(48.25, 42.25) * mm, "end": v(48.25, 48.25) * mm});
            skLineSegment(sketch, "E86.1", {"start": v(48.25, 48.25) * mm, "end": v(42.25, 48.25) * mm});
            skLineSegment(sketch, "E87.0", {"start": v(55.75, -55.75) * mm, "end": v(55.75, 55.75) * mm});
            skLineSegment(sketch, "E88.0", {"start": v(-48.25, -42.25) * mm, "end": v(-48.25, -48.25) * mm});
            skLineSegment(sketch, "E89.0", {"start": v(-48.25, -48.25) * mm, "end": v(-42.25, -48.25) * mm});
            skLineSegment(sketch, "E90.0", {"start": v(-55.75, -55.75) * mm, "end": v(55.75, -55.75) * mm});
            skLineSegment(sketch, "E91.0", {"start": v(48.25, -42.25) * mm, "end": v(48.25, -48.25) * mm});
            skLineSegment(sketch, "E91.1", {"start": v(48.25, -48.25) * mm, "end": v(42.25, -48.25) * mm});
            skLineSegment(sketch, "E92.bottom", {"start": v(-48.25, -48.25) * mm, "end": v(-55.75, -48.25) * mm, "construction": true});
            skLineSegment(sketch, "E92.top", {"start": v(-48.25, -55.75) * mm, "end": v(-55.75, -55.75) * mm, "construction": true});
            skLineSegment(sketch, "E92.left", {"start": v(-48.25, -48.25) * mm, "end": v(-48.25, -55.75) * mm, "construction": true});
            skLineSegment(sketch, "E92.right", {"start": v(-55.75, -48.25) * mm, "end": v(-55.75, -55.75) * mm, "construction": true});
            skLineSegment(sketch, "E93.bottom", {"start": v(48.25, -48.25) * mm, "end": v(55.75, -48.25) * mm, "construction": true});
            skLineSegment(sketch, "E93.top", {"start": v(48.25, -55.75) * mm, "end": v(55.75, -55.75) * mm, "construction": true});
            skLineSegment(sketch, "E93.left", {"start": v(48.25, -48.25) * mm, "end": v(48.25, -55.75) * mm, "construction": true});
            skLineSegment(sketch, "E93.right", {"start": v(55.75, -48.25) * mm, "end": v(55.75, -55.75) * mm, "construction": true});
            skLineSegment(sketch, "E94.bottom", {"start": v(48.25, 48.25) * mm, "end": v(55.75, 48.25) * mm, "construction": true});
            skLineSegment(sketch, "E94.top", {"start": v(48.25, 55.75) * mm, "end": v(55.75, 55.75) * mm, "construction": true});
            skLineSegment(sketch, "E94.left", {"start": v(48.25, 48.25) * mm, "end": v(48.25, 55.75) * mm, "construction": true});
            skLineSegment(sketch, "E94.right", {"start": v(55.75, 48.25) * mm, "end": v(55.75, 55.75) * mm, "construction": true});
            skLineSegment(sketch, "E95", {"start": v(-55.75, -52) * mm, "end": v(55.75, -52) * mm, "construction": true});
            skLineSegment(sketch, "E96", {"start": v(52, -55.75) * mm, "end": v(52, 55.75) * mm, "construction": true});
            skLineSegment(sketch, "E97", {"start": v(-52, 55.75) * mm, "end": v(-52, -55.75) * mm, "construction": true});
            skLineSegment(sketch, "E98", {"start": v(-55.75, 52) * mm, "end": v(55.75, 52) * mm, "construction": true});
            skCircle(sketch, "E99", {"center": v(-52, 52) * mm, "radius": 1.7 * mm});
            skCircle(sketch, "E100", {"center": v(-52, 52) * mm, "radius": 3.03 * mm});
            skLineSegment(sketch, "E101", {"start": v(0, 52) * mm, "end": v(0, -52) * mm, "construction": true});
            skLineSegment(sketch, "E102", {"start": v(-52, 0) * mm, "end": v(52, 0) * mm, "construction": true});
            skCircle(sketch, "E103.MirrorC", {"center": v(52, 52) * mm, "radius": 1.7 * mm});
            skCircle(sketch, "E104.MirrorC", {"center": v(52, 52) * mm, "radius": 3.03 * mm});
            skCircle(sketch, "E105.MirrorC", {"center": v(52, -52) * mm, "radius": 1.7 * mm});
            skCircle(sketch, "E106.MirrorC", {"center": v(52, -52) * mm, "radius": 3.03 * mm});
            skCircle(sketch, "E107.MirrorC", {"center": v(-52, -52) * mm, "radius": 3.03 * mm});
            skCircle(sketch, "E108.MirrorC", {"center": v(-52, -52) * mm, "radius": 1.7 * mm});
            skSolve(sketch);
        }
        {
            var Q0;
            Q0=makeQuery(id+"F26.imprint","IMPRINT",FACE,{"disambiguationData":[TD([[makeQuery(id+"F26.imprint","IMPRINT",EDGE,{"derivedFrom":sQuery(id+"F26.wireOp",EDGE,"E108.MirrorC")}),-1.0]])]});
            var Q1;
            Q1=makeQuery(id+"F26.imprint","IMPRINT",FACE,{"disambiguationData":[TD([[makeQuery(id+"F26.imprint","IMPRINT",EDGE,{"derivedFrom":sQuery(id+"F26.wireOp",EDGE,"E105.MirrorC")}),1.0]])]});
            var Q2;
            Q2=makeQuery(id+"F26.imprint","IMPRINT",FACE,{"disambiguationData":[TD([[makeQuery(id+"F26.imprint","IMPRINT",EDGE,{"derivedFrom":sQuery(id+"F26.wireOp",EDGE,"E103.MirrorC")}),-1.0]])]});
            var Q3;
            Q3=makeQuery(id+"F26.imprint","IMPRINT",FACE,{"disambiguationData":[TD([[makeQuery(id+"F26.imprint","IMPRINT",EDGE,{"derivedFrom":sQuery(id+"F26.wireOp",EDGE,"E99")}),1.0]])]});
            extrude(context, id + "F27", {"entities" : qUnion([Q0, Q1, Q2, Q3]), "operationType" : NewBodyOperationType.REMOVE, "oppositeDirection" : true, "depth" : (getVariable(context, 'topThickness')) * mm});
        }
        {
            var Q0;
            Q0=makeQuery(id+"F26.imprint","IMPRINT",FACE,{"disambiguationData":[TD([[makeQuery(id+"F26.imprint","IMPRINT",EDGE,{"derivedFrom":sQuery(id+"F26.wireOp",EDGE,"E99")}),-1.0]])]});
            var Q1;
            Q1=makeQuery(id+"F26.imprint","IMPRINT",FACE,{"disambiguationData":[TD([[makeQuery(id+"F26.imprint","IMPRINT",EDGE,{"derivedFrom":sQuery(id+"F26.wireOp",EDGE,"E103.MirrorC")}),1.0]])]});
            var Q2;
            Q2=makeQuery(id+"F26.imprint","IMPRINT",FACE,{"disambiguationData":[TD([[makeQuery(id+"F26.imprint","IMPRINT",EDGE,{"derivedFrom":sQuery(id+"F26.wireOp",EDGE,"E107.MirrorC")}),-1.0]])]});
            var Q3;
            Q3=makeQuery(id+"F26.imprint","IMPRINT",FACE,{"disambiguationData":[TD([[makeQuery(id+"F26.imprint","IMPRINT",EDGE,{"derivedFrom":sQuery(id+"F26.wireOp",EDGE,"E105.MirrorC")}),-1.0]])]});
            extrude(context, id + "F28", {"entities" : qUnion([Q0, Q1, Q2, Q3]), "operationType" : NewBodyOperationType.REMOVE, "oppositeDirection" : true, "depth" : (getVariable(context, 'screwHeadDepth') + getVariable(context, 'screwHeadRecessTolerance')) * mm});
        }
        {
            var Q0;
            Q0=makeQuery(id+"F28.boolean.opBoolean","COPY",FACE,{"derivedFrom":makeQuery(id+"F28.opExtrude","CAP_FACE",FACE,{"disambiguationData":[OSD([sQuery(id+"F26.wireOp",EDGE,"E107.MirrorC"),sQuery(id+"F26.wireOp",EDGE,"E108.MirrorC")])],"isStart":false})});
            var sketch = newSketch(context, id + "F29", { "sketchPlane" : qUnion([Q0])});
            skLineSegment(sketch, "E109.0", {"start": v(-55.75, -55.75) * mm, "end": v(55.75, -55.75) * mm});
            skLineSegment(sketch, "E109.1", {"start": v(-55.75, 55.75) * mm, "end": v(-55.75, -55.75) * mm});
            skLineSegment(sketch, "E109.2", {"start": v(55.75, 55.75) * mm, "end": v(-55.75, 55.75) * mm});
            skLineSegment(sketch, "E109.3", {"start": v(55.75, -55.75) * mm, "end": v(55.75, 55.75) * mm});
            skSolve(sketch);
        }
        {
            var Q0;
            Q0 = qSketchRegion(id + "F29", true);
            extrude(context, id + "F30", {"entities" : qUnion([Q0]), "operationType" : NewBodyOperationType.ADD, "oppositeDirection" : true, "depth" : (getVariable(context, 'screwHeadSupportThickness')) * mm});
        }
        {
            var Q0;
            {var subQ2=sQuery(id+"F15.wireOp",EDGE,"E12");var subQ7=sQuery(id+"F13.wireOp",EDGE,"E0.top");var subQ10=sQuery(id+"F13.wireOp",EDGE,"E0.right");Q0=makeQuery(id+"F16.boolean.opBoolean","SPLIT",FACE,{"disambiguationData":[TD([makeQuery(id+"F16.opExtrude","SWEPT_FACE",FACE,{"disambiguationData":[OSD([subQ2])]})])],"derivedFrom":makeQuery(id+"F14.opExtrude","CAP_FACE",FACE,{"disambiguationData":[OSD([sQuery(id+"F13.wireOp",EDGE,"E0.bottom"),subQ7,sQuery(id+"F13.wireOp",EDGE,"E0.left"),subQ10])],"isStart":false})});}
            var sketch = newSketch(context, id + "F31", { "sketchPlane" : qUnion([Q0])});
            skLineSegment(sketch, "E110.0", {"start": v(-55.75, 52) * mm, "end": v(55.75, 52) * mm, "construction": true});
            skLineSegment(sketch, "E111.0", {"start": v(-52, 0) * mm, "end": v(52, 0) * mm, "construction": true});
            skLineSegment(sketch, "E112.0", {"start": v(0, 52) * mm, "end": v(0, -52) * mm, "construction": true});
            skLineSegment(sketch, "E113.0", {"start": v(52, -55.75) * mm, "end": v(52, 55.75) * mm, "construction": true});
            skLineSegment(sketch, "E114.0", {"start": v(-52, 55.75) * mm, "end": v(-52, -55.75) * mm, "construction": true});
            skLineSegment(sketch, "E115.0", {"start": v(-55.75, -52) * mm, "end": v(55.75, -52) * mm, "construction": true});
            skCircle(sketch, "E116", {"center": v(-52, 52) * mm, "radius": 1.6 * mm});
            skCircle(sketch, "E117.MirrorC", {"center": v(52, 52) * mm, "radius": 1.6 * mm});
            skCircle(sketch, "E118.MirrorC", {"center": v(52, -52) * mm, "radius": 1.6 * mm});
            skCircle(sketch, "E119.MirrorC", {"center": v(-52, -52) * mm, "radius": 1.6 * mm});
            skSolve(sketch);
        }
        {
            var Q0;
            Q0 = qSketchRegion(id + "F31", true);
            extrude(context, id + "F32", {"entities" : qUnion([Q0]), "operationType" : NewBodyOperationType.REMOVE, "oppositeDirection" : true, "depth" : (((getVariable(context, 'screwThreadDepth') + getVariable(context, 'screwHeadDepth')) - getVariable(context, 'topThickness')) + getVariable(context, 'screwThreadExtraDepth')) * mm});
        }
        {
            var Q0;
            Q0=makeQuery(id+"F17.imprint","IMPRINT",FACE,{"disambiguationData":[TD([[makeQuery(id+"F17.imprint","IMPRINT",EDGE,{"derivedFrom":sQuery(id+"F17.wireOp",EDGE,"E68.bottom")}),-1.0]])]});
            extrude(context, id + "F33", {"entities" : qUnion([Q0]), "operationType" : NewBodyOperationType.REMOVE, "depth" : (getVariable(context, 'baseThickness') - getVariable(context, 'shellThickness')) * mm});
        }
        {
            var Q0;
            Q0=makeQuery(id+"F22.opExtrude","CAP_FACE",FACE,{"disambiguationData":[OSD([sQuery(id+"F21.wireOp",EDGE,"E70.0"),sQuery(id+"F21.wireOp",EDGE,"E70.1"),sQuery(id+"F21.wireOp",EDGE,"E70.2"),sQuery(id+"F21.wireOp",EDGE,"E70.3"),sQuery(id+"F21.wireOp",EDGE,"E71.0"),sQuery(id+"F21.wireOp",EDGE,"E71.1"),sQuery(id+"F21.wireOp",EDGE,"E71.2"),sQuery(id+"F21.wireOp",EDGE,"E71.3"),sQuery(id+"F21.wireOp",EDGE,"E72.0"),sQuery(id+"F21.wireOp",EDGE,"E72.1"),sQuery(id+"F21.wireOp",EDGE,"E73.0"),sQuery(id+"F21.wireOp",EDGE,"E74.0"),sQuery(id+"F21.wireOp",EDGE,"E75.0"),sQuery(id+"F21.wireOp",EDGE,"E75.1"),sQuery(id+"F21.wireOp",EDGE,"E75.2"),sQuery(id+"F21.wireOp",EDGE,"E75.3"),sQuery(id+"F21.wireOp",EDGE,"E76.0"),sQuery(id+"F21.wireOp",EDGE,"E77.0"),sQuery(id+"F21.wireOp",EDGE,"E78.0"),sQuery(id+"F21.wireOp",EDGE,"E79.0")])],"isStart":true});
            var sketch = newSketch(context, id + "F34", { "sketchPlane" : qUnion([Q0])});
            skLineSegment(sketch, "E120.0", {"start": v(-48.25, -48.25) * mm, "end": v(-48.25, 48.25) * mm});
            skLineSegment(sketch, "E120.1", {"start": v(48.25, 48.25) * mm, "end": v(-48.25, 48.25) * mm});
            skLineSegment(sketch, "E120.2", {"start": v(48.25, -48.25) * mm, "end": v(48.25, 48.25) * mm});
            skLineSegment(sketch, "E120.3", {"start": v(48.25, -48.25) * mm, "end": v(-48.25, -48.25) * mm});
            skSolve(sketch);
        }
        {
            var Q0;
            Q0 = qSketchRegion(id + "F34", true);
            extrude(context, id + "F35", {"entities" : qUnion([Q0]), "operationType" : NewBodyOperationType.REMOVE, "oppositeDirection" : true, "depth" : (getVariable(context, 'topThickness') - getVariable(context, 'shellThickness')) * mm});
        }
        {
            var Q0;
            Q0=makeQuery(id+"F20.opExtrude","CAP_FACE",FACE,{"disambiguationData":[OSD([sQuery(id+"F19.wireOp",EDGE,"E69.bottom"),sQuery(id+"F19.wireOp",EDGE,"E69.top"),sQuery(id+"F19.wireOp",EDGE,"E69.left"),sQuery(id+"F19.wireOp",EDGE,"E69.right")])],"isStart":false});
            var sketch = newSketch(context, id + "F36", { "sketchPlane" : qUnion([Q0])});
            skLineSegment(sketch, "E121.bottom", {"start": v(-46.8, 89.13) * mm, "end": v(43.2, 89.13) * mm});
            skLineSegment(sketch, "E121.top", {"start": v(-46.8, 179.13) * mm, "end": v(43.2, 179.13) * mm});
            skLineSegment(sketch, "E121.left", {"start": v(-46.8, 89.13) * mm, "end": v(-46.8, 179.13) * mm});
            skLineSegment(sketch, "E121.right", {"start": v(43.2, 89.13) * mm, "end": v(43.2, 179.13) * mm});
            skCircle(sketch, "E122", {"center": v(20.52, 111.8) * mm, "radius": 4.12 * mm});
            skSolve(sketch);
        }
        {
            var Q0;
            Q0=makeQuery(id+"F36.imprint","IMPRINT",FACE,{"disambiguationData":[TD([[makeQuery(id+"F36.imprint","IMPRINT",EDGE,{"derivedFrom":sQuery(id+"F36.wireOp",EDGE,"E121.bottom")}),1.0]])]});
            extrude(context, id + "F37", {"entities" : qUnion([Q0]), "oppositeDirection" : true, "depth" : (getVariable(context, 'lithophaneThickness')) * mm});
        }
    });
